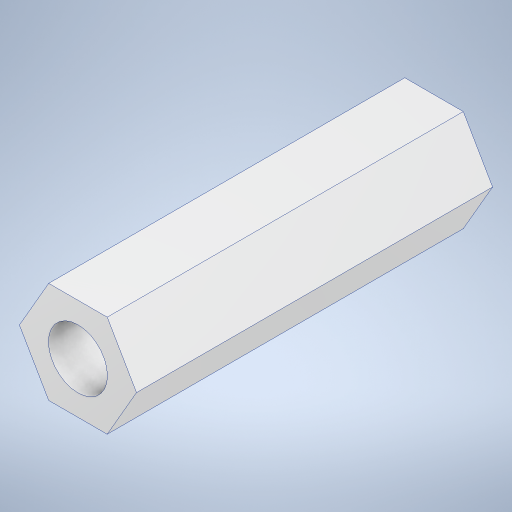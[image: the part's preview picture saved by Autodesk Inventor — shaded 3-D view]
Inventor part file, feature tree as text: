
AUTODESK INVENTOR PART (.ipt)
format: ipt  version: 2024 (Build 280153000, 153)  size: 216,576 bytes
history: native  units: in
note: dims shown in document units (in); Inventor stores cm internally (conversion verified against a paired STEP export)
features: extrude x1, sketch x1
ambient origin geometry x8: Origin, YZ Plane, XZ Plane, XY Plane, X Axis, Y Axis, Z Axis, Center Point
bodies: Solid1 (feature_tree)
feature tree (2):
  extrude  "Extrusion1"  Depth=1.756in
  sketch  "Sketch1"  dims[d0=0.5in d1=0.291in d2=1.756in d3=0.0in]
